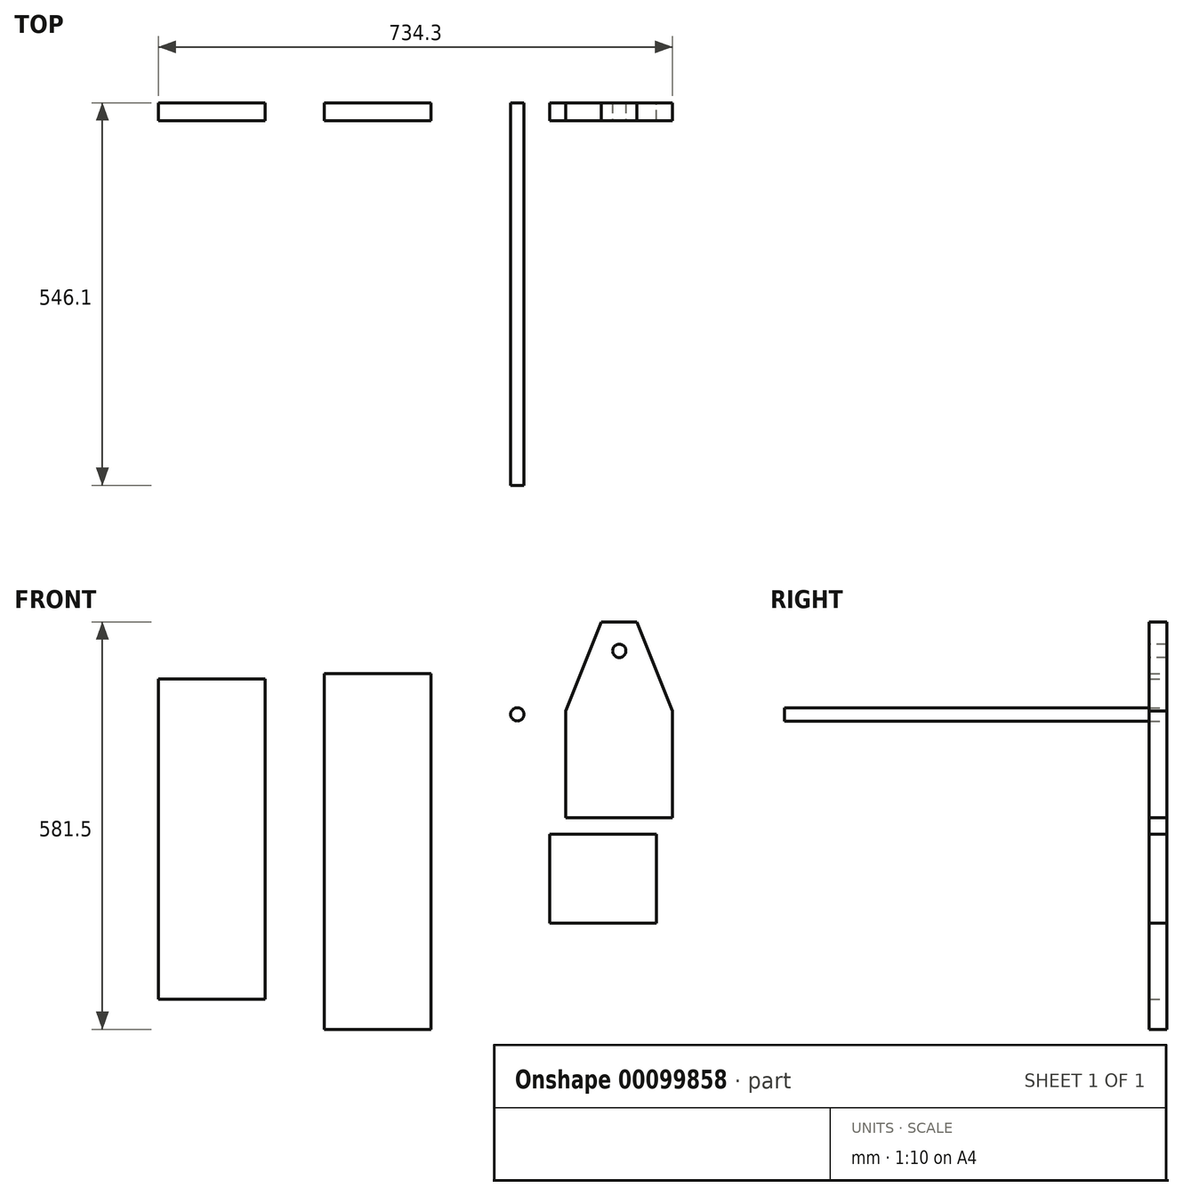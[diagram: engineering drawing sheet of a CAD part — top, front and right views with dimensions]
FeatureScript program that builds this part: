
annotation { "Feature Type Name" : "Feature", "Feature Type Description" : "" }
export const myFeature = defineFeature(function(context is Context, id is Id, definition is map)
    precondition{}
    {
        {
            var Q0;
            Q0=qCreatedBy(makeId("Front.planeOp"),FACE);
            var sketch = newSketch(context, id + "F0", { "sketchPlane" : qUnion([Q0])});
            skLineSegment(sketch, "E0", {"start": v(-135.55, 246.96) * mm, "end": v(-135.55, -261.04) * mm});
            skLineSegment(sketch, "E1", {"start": v(-135.55, -261.04) * mm, "end": v(16.85, -261.04) * mm});
            skLineSegment(sketch, "E2", {"start": v(16.85, -261.04) * mm, "end": v(16.85, 246.96) * mm});
            skLineSegment(sketch, "E3", {"start": v(16.85, 246.96) * mm, "end": v(-135.55, 246.96) * mm});
            skLineSegment(sketch, "E4", {"start": v(-372.26, 238.88) * mm, "end": v(-372.26, -218.32) * mm});
            skLineSegment(sketch, "E5", {"start": v(-372.26, -218.32) * mm, "end": v(-219.86, -218.32) * mm});
            skLineSegment(sketch, "E6", {"start": v(-219.86, -218.32) * mm, "end": v(-219.86, 238.88) * mm});
            skLineSegment(sketch, "E7", {"start": v(-219.86, 238.88) * mm, "end": v(-372.26, 238.88) * mm});
            skLineSegment(sketch, "E8", {"start": v(186.54, 17.2) * mm, "end": v(338.94, 17.2) * mm});
            skLineSegment(sketch, "E9", {"start": v(338.94, 17.2) * mm, "end": v(338.94, -109.8) * mm});
            skLineSegment(sketch, "E10", {"start": v(338.94, -109.8) * mm, "end": v(186.54, -109.8) * mm});
            skLineSegment(sketch, "E11", {"start": v(186.54, -109.8) * mm, "end": v(186.54, 17.2) * mm});
            skLineSegment(sketch, "E12", {"start": v(209.64, 320.46) * mm, "end": v(362.04, 320.46) * mm});
            skLineSegment(sketch, "E13", {"start": v(362.04, 320.46) * mm, "end": v(362.04, 41.06) * mm});
            skLineSegment(sketch, "E14", {"start": v(362.04, 41.06) * mm, "end": v(209.64, 41.06) * mm});
            skLineSegment(sketch, "E15", {"start": v(209.64, 41.06) * mm, "end": v(209.64, 320.46) * mm});
            skCircle(sketch, "E16", {"center": v(140.2, 188.6) * mm, "radius": 9.53 * mm});
            skSolve(sketch);
        }
        {
            var Q0;
            Q0=makeQuery(id+"F0.imprint","IMPRINT",FACE,{"disambiguationData":[TD([[makeQuery(id+"F0.imprint","IMPRINT",EDGE,{"derivedFrom":sQuery(id+"F0.wireOp",EDGE,"E4")}),1.0]])]});
            var Q1;
            Q1=makeQuery(id+"F0.imprint","IMPRINT",FACE,{"disambiguationData":[TD([[makeQuery(id+"F0.imprint","IMPRINT",EDGE,{"derivedFrom":sQuery(id+"F0.wireOp",EDGE,"E0")}),1.0]])]});
            var Q2;
            Q2=makeQuery(id+"F0.imprint","IMPRINT",FACE,{"disambiguationData":[TD([[makeQuery(id+"F0.imprint","IMPRINT",EDGE,{"derivedFrom":sQuery(id+"F0.wireOp",EDGE,"t4Jxa8Hb-KSBL-P3sA-lekm-M2hDN2ZlX5ae")}),1.0]])]});
            var Q3;
            Q3=makeQuery(id+"F0.imprint","IMPRINT",FACE,{"disambiguationData":[TD([[makeQuery(id+"F0.imprint","IMPRINT",EDGE,{"derivedFrom":sQuery(id+"F0.wireOp",EDGE,"E8")}),-1.0]])]});
            var Q4;
            Q4=makeQuery(id+"F0.imprint","IMPRINT",FACE,{"disambiguationData":[TD([[makeQuery(id+"F0.imprint","IMPRINT",EDGE,{"derivedFrom":sQuery(id+"F0.wireOp",EDGE,"E12")}),-1.0]])]});
            extrude(context, id + "F1", {"entities" : qUnion([Q0, Q1, Q2, Q3, Q4]), "depth" : 25.4 * mm});
        }
        {
            var Q0;
            Q0=makeQuery(id+"F1.opExtrude","SWEPT_EDGE",EDGE,{"disambiguationData":[OSD([sQuery(id+"F0.wireOp",EDGE,"E12"),sQuery(id+"F0.wireOp",EDGE,"E13")])]});
            var Q1;
            Q1=makeQuery(id+"F1.opExtrude","SWEPT_EDGE",EDGE,{"disambiguationData":[OSD([sQuery(id+"F0.wireOp",EDGE,"E12"),sQuery(id+"F0.wireOp",EDGE,"E15")])]});
            chamfer(context, id + "F2", {"entities" : qUnion([Q0, Q1]), "chamferType" : ChamferType.TWO_OFFSETS, "width1" : 127 * mm, "oppositeDirection" : true, "width2" : 50.8 * mm, "tangentPropagation" : true});
        }
        {
            var Q0;
            Q0=makeQuery(id+"F1.opExtrude","CAP_FACE",FACE,{"disambiguationData":[OSD([sQuery(id+"F0.wireOp",EDGE,"E12"),sQuery(id+"F0.wireOp",EDGE,"E13"),sQuery(id+"F0.wireOp",EDGE,"E14"),sQuery(id+"F0.wireOp",EDGE,"E15")])],"isStart":false});
            var sketch = newSketch(context, id + "F3", { "sketchPlane" : qUnion([Q0])});
            skCircle(sketch, "E17", {"center": v(285.84, 279.19) * mm, "radius": 9.53 * mm});
            skPoint(sketch, "E17.centerSnap0", {"position": v(285.84, 41.06) * mm});
            skSolve(sketch);
        }
        {
            var Q0;
            Q0=makeQuery(id+"F3.imprint","IMPRINT",FACE,{"disambiguationData":[TD([[makeQuery(id+"F3.imprint","IMPRINT",EDGE,{"derivedFrom":sQuery(id+"F3.wireOp",EDGE,"E17")}),1.0]])]});
            extrude(context, id + "F4", {"entities" : qUnion([Q0]), "operationType" : NewBodyOperationType.REMOVE, "oppositeDirection" : true, "depth" : 25.4 * mm});
        }
        {
            var Q0;
            Q0=makeQuery(id+"F0.imprint","IMPRINT",FACE,{"disambiguationData":[TD([[makeQuery(id+"F0.imprint","IMPRINT",EDGE,{"derivedFrom":sQuery(id+"F0.wireOp",EDGE,"E16")}),1.0]])]});
            extrude(context, id + "F5", {"entities" : qUnion([Q0]), "depth" : 546.1 * mm});
        }
    });
